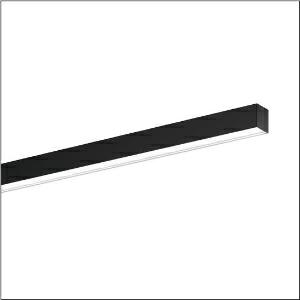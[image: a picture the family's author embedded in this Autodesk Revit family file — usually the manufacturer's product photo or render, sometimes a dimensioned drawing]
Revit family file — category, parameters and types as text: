
# Revit family: silica_21_51mx20dc35bb
name_source: partatom
category: Lighting Fixtures
units: mm (PartAtom-declared; Revit-internal decimal feet)

## family parameters
Cut with Voids When Loaded = No
Host = Face
Light Source = No
Part Type = Normal
Room Calculation Point = No
Round Connector Dimension = Use Diameter
Shared = No

## types (1)
- --- (1 x LED, 6000 lm, 42.6 W, 3000K)
    Apparent Load = 43 VA
    CIE Flux Codes = 48 79 96 100 100
    Color Rendering = 80
    Color Temperature = 3000K
    Default Elevation = 1800 mm
    Description = Silica 21, office luminaire, primary optical cover: cover, of PMMA, opal, light emission: direct distribution, primary light characteristic: symmetric, installation type: surface-mounted, LED, rated luminous flux: 6.000lm, luminous efficacy: 141lm/W, light colour: 830, colour temperature: 3000K, control gear: DALI 2, with terminal, 3+2-pole, max. 2.5mm², mains connection: 220..240V, AC, 50/60Hz, rated input power: 42.6W, luminaire housing, of aluminium, matt jet black (RAL 9005), length: 3.004mm, width: 53mm, height: 53mm, protection rating (complete): IP20, insulation class (complete): insulation class I (protective earthing), certification: CE, permissible operating ambient temperature: 0..+35°C, standard: EN 50419, packaging unit: 1 piece
    Height = 53 mm
    Lamp = 1 x LED
    Lamp Light Flux = 6000 lm
    Lamp Power = 42.6 W
    Lamp count = 1
    Length = 3004 mm
    Luminous efficacy = 141 lm/W
    Manufacturer = Siteco
    ModVariant = No
    Model = 51MX20DC35BB
    Mounting Place = Ceiling
    Mounting Type = Surface mounted
    Number of Poles = 1
    OnlyDefault = Yes
    Power Factor = 1
    Product Name = Silica 21
    Product group = office luminaire | ceiling mounted
    ProductGroupID = 301
    Protection Class = Protection class I
    Protection Degree = IP 20
    RLX_Detail_Level = 1
    RLX_Emergency_Light_Flux = 0 lm
    RLX_Emergency_Type = 0
    RLX_Emergency_Type_DB = No
    RlxData = <blob elided: 28865 chars, md5=34442136>
    Socket = socket
    Standby Power = 0 W
    System Light Flux = 6000 lm
    System Power = 43 W
    Type Comments = factory setting: luminous flux: 100 % | dim-lin: 254 | 233 mA
    Type Image = l_1335925.jpg
    URL = http://relux.com
    VarID = @adj_119525
    Voltage = 0 V
    Weight = 0.00 kg
    Width = 53 mm

## geometry (parser evidence)
native form markers: Blend x4, Sweep x9
no freeform markers — native parametric forms only
